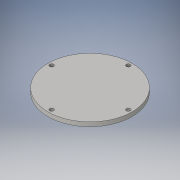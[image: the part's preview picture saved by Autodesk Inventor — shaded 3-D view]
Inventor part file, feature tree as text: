
AUTODESK INVENTOR PART (.ipt)
format: ipt  version: 2016 (Build 200138000, 138)  size: 101,888 bytes
history: native  units: in
note: dims shown in document units (in); Inventor stores cm internally (conversion verified against a paired STEP export)
features: sketch x2, extrude x1, hole x1
ambient origin geometry x8: Origin, YZ Plane, XZ Plane, XY Plane, X Axis, Y Axis, Z Axis, Center Point
bodies: Solid1 (feature_tree)
feature tree (4):
  extrude  "Extrusion1"  Depth=0.125in TaperAngle=0.0deg
  hole  "Hole1"  [1 undecoded]
  sketch  "Sketch1"  dims[d0=2.5in d1=0.125in d2=0.0in]
  sketch  "Sketch2"  dims[d3=1.14in d4=1.5748in d6=360.0deg d8=0.1181in d9=0.75in d10=0.375in d11=0.25in d12=0.5635in d13=1.0in d14=0.8108in]
note: 1 required parameter value undecoded (feature->parameter linkage not recoverable at this tier; creation-order binding heuristic only, values carry confidence <= 0.55)
